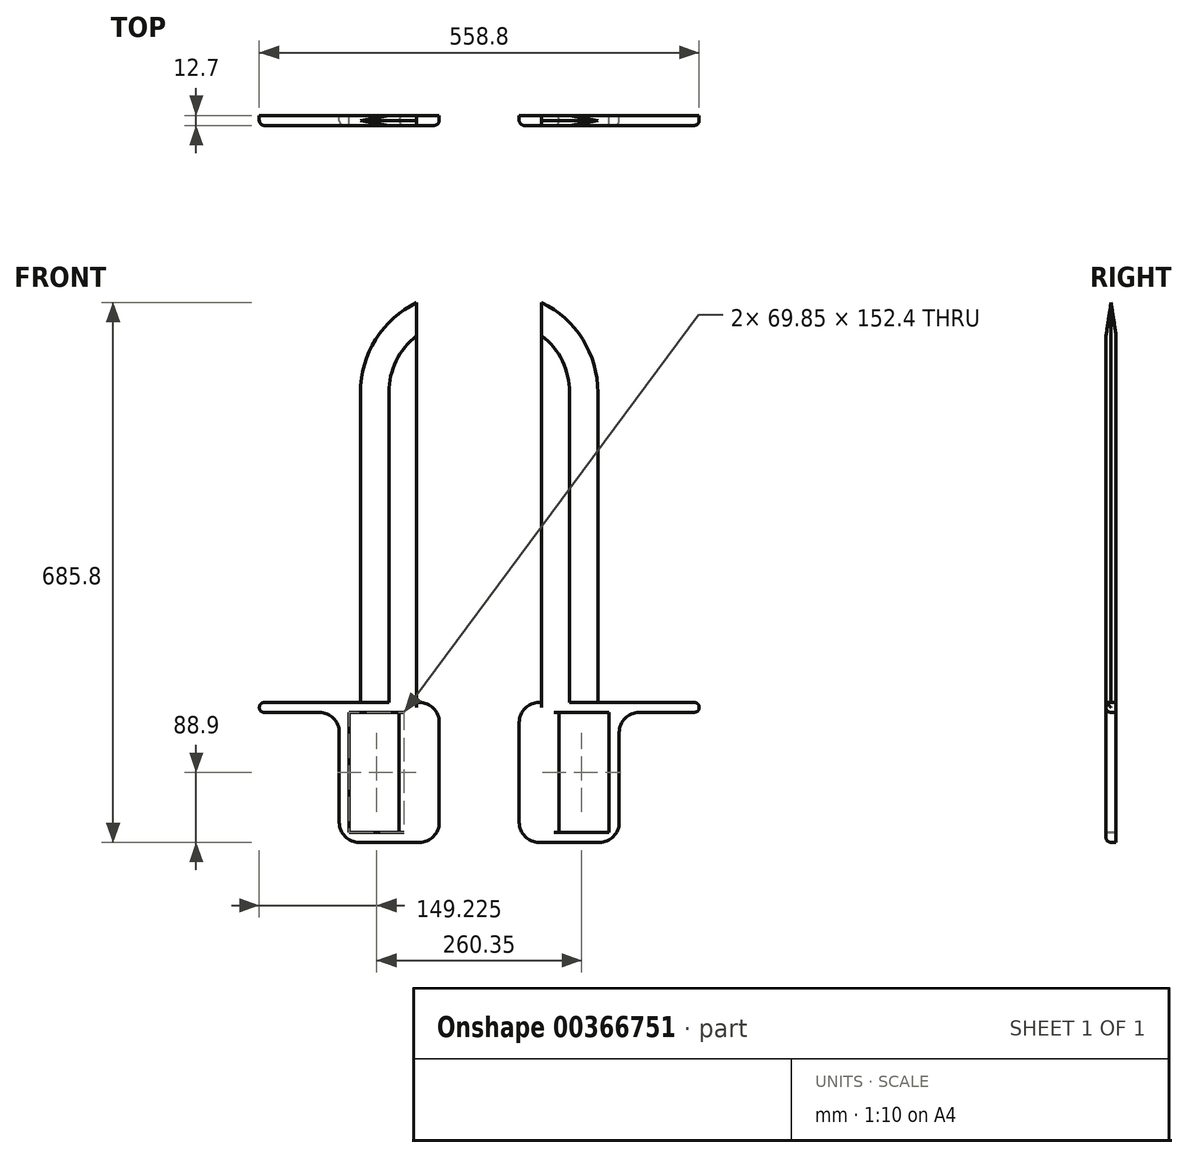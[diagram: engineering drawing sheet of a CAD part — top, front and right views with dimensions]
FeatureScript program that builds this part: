
annotation { "Feature Type Name" : "Feature", "Feature Type Description" : "" }
export const myFeature = defineFeature(function(context is Context, id is Id, definition is map)
    precondition{}
    {
        {
            var Q0;
            Q0=qCreatedBy(makeId("Front.planeOp"),FACE);
            var sketch = newSketch(context, id + "F0", { "sketchPlane" : qUnion([Q0])});
            skLineSegment(sketch, "E0", {"start": v(0, 0) * mm, "end": v(-76.2, 0) * mm});
            skLineSegment(sketch, "E1.bottom", {"start": v(-50.8, -76.2) * mm, "end": v(-101.6, -76.2) * mm});
            skLineSegment(sketch, "E1.top", {"start": v(-50.8, 76.2) * mm, "end": v(-101.6, 76.2) * mm});
            skLineSegment(sketch, "E1.left", {"start": v(-50.8, -76.2) * mm, "end": v(-50.8, 76.2) * mm});
            skLineSegment(sketch, "E1.right", {"start": v(-101.6, -76.2) * mm, "end": v(-101.6, 76.2) * mm});
            skPoint(sketch, "E1.middle", {"position": v(-76.2, 0) * mm});
            skLineSegment(sketch, "E2", {"start": v(-50.8, 76.2) * mm, "end": v(-50.8, 88.9) * mm});
            skLineSegment(sketch, "E3", {"start": v(-50.8, 88.9) * mm, "end": v(-177.8, 88.9) * mm});
            skLineSegment(sketch, "E4", {"start": v(-101.6, 76.2) * mm, "end": v(-165.1, 76.2) * mm});
            skLineSegment(sketch, "E5", {"start": v(-177.8, 88.9) * mm, "end": v(-177.8, -88.9) * mm});
            skLineSegment(sketch, "E6", {"start": v(-165.1, 76.2) * mm, "end": v(-165.1, -76.2) * mm});
            skLineSegment(sketch, "E7", {"start": v(-165.1, -76.2) * mm, "end": v(-101.6, -76.2) * mm});
            skLineSegment(sketch, "E8", {"start": v(-177.8, -88.9) * mm, "end": v(-50.8, -88.9) * mm});
            skLineSegment(sketch, "E9", {"start": v(-50.8, -76.2) * mm, "end": v(-50.8, -88.9) * mm});
            skLineSegment(sketch, "E10", {"start": v(-165.1, 76.2) * mm, "end": v(-279.4, 76.2) * mm});
            skLineSegment(sketch, "E11", {"start": v(-177.8, 88.9) * mm, "end": v(-279.4, 88.9) * mm});
            skLineSegment(sketch, "E12", {"start": v(-279.4, 88.9) * mm, "end": v(-279.4, 76.2) * mm});
            skSolve(sketch);
        }
        {
            var Q0;
            Q0 = qSketchRegion(id + "F0", true);
            extrude(context, id + "F1", {"entities" : qUnion([Q0]), "depth" : 12.7 * mm});
        }
        {
            var Q0;
            Q0=makeQuery(id+"F1.opExtrude","CAP_FACE",FACE,{"disambiguationData":[OSD([sQuery(id+"F0.wireOp",EDGE,"E1.left"),sQuery(id+"F0.wireOp",EDGE,"E1.right"),sQuery(id+"F0.wireOp",EDGE,"E2"),sQuery(id+"F0.wireOp",EDGE,"E3"),sQuery(id+"F0.wireOp",EDGE,"E4"),sQuery(id+"F0.wireOp",EDGE,"E5"),sQuery(id+"F0.wireOp",EDGE,"E6"),sQuery(id+"F0.wireOp",EDGE,"E7"),sQuery(id+"F0.wireOp",EDGE,"E8"),sQuery(id+"F0.wireOp",EDGE,"E9")])],"isStart":false});
            var sketch = newSketch(context, id + "F2", { "sketchPlane" : qUnion([Q0])});
            skLineSegment(sketch, "E13", {"start": v(-50.8, 88.9) * mm, "end": v(-50.8, 88.9) * mm});
            skLineSegment(sketch, "E14", {"start": v(-50.8, 88.9) * mm, "end": v(-165.1, 88.9) * mm});
            skLineSegment(sketch, "E15", {"start": v(-165.1, 88.9) * mm, "end": v(-107.95, 88.9) * mm});
            skLineSegment(sketch, "E16", {"start": v(-50.8, 88.9) * mm, "end": v(-107.95, 88.9) * mm});
            skLineSegment(sketch, "E17", {"start": v(-107.95, 88.9) * mm, "end": v(-50.8, 88.9) * mm});
            skLineSegment(sketch, "E18", {"start": v(-79.37, 88.9) * mm, "end": v(-107.95, 88.9) * mm});
            skLineSegment(sketch, "E19", {"start": v(-50.8, 88.9) * mm, "end": v(-79.37, 88.9) * mm});
            skLineSegment(sketch, "E20", {"start": v(-79.37, 88.9) * mm, "end": v(-79.37, 596.9) * mm});
            skLineSegment(sketch, "E21", {"start": v(-79.37, 596.9) * mm, "end": v(-79.37, 596.9) * mm});
            skLineSegment(sketch, "E22", {"start": v(-107.95, 88.9) * mm, "end": v(-136.52, 88.9) * mm});
            skLineSegment(sketch, "E23", {"start": v(-136.52, 88.9) * mm, "end": v(-165.1, 88.9) * mm});
            skLineSegment(sketch, "E24", {"start": v(-165.1, 88.9) * mm, "end": v(-150.81, 88.9) * mm});
            skLineSegment(sketch, "E25", {"start": v(-150.81, 88.9) * mm, "end": v(-150.81, 596.9) * mm});
            skLineSegment(sketch, "E26", {"start": v(-79.37, 596.9) * mm, "end": v(-150.81, 596.9) * mm});
            skSolve(sketch);
        }
        {
            var Q0;
            Q0 = qSketchRegion(id + "F2", true);
            extrude(context, id + "F3", {"entities" : qUnion([Q0]), "operationType" : NewBodyOperationType.ADD, "depth" : -12.7 * mm});
        }
        {
            var Q0;
            Q0=makeQuery(id+"F3.opExtrude","SWEPT_EDGE",EDGE,{"disambiguationData":[OSD([sQuery(id+"F2.wireOp",EDGE,"E25"),sQuery(id+"F2.wireOp",EDGE,"E26")])]});
            fillet(context, id + "F4", {"entities" : qUnion([Q0]), "radius" : 127 * mm, "tangentPropagation" : true, "allowEdgeOverflow" : false});
        }
        {
            var Q0;
            Q0=makeQuery(id+"F1.opExtrude","CAP_EDGE",EDGE,{"disambiguationData":[OSD([sQuery(id+"F0.wireOp",EDGE,"E1.right")])],"isStart":false});
            var Q1;
            Q1=makeQuery(id+"F1.opExtrude","CAP_EDGE",EDGE,{"disambiguationData":[OSD([sQuery(id+"F0.wireOp",EDGE,"E1.right")])],"isStart":true});
            fillet(context, id + "F5", {"entities" : qUnion([Q0, Q1]), "radius" : 6.35 * mm, "tangentPropagation" : true, "allowEdgeOverflow" : false});
        }
        {
            var Q0;
            Q0=makeQuery(id+"F1.opExtrude","SWEPT_EDGE",EDGE,{"disambiguationData":[OSD([sQuery(id+"F0.wireOp",EDGE,"E3"),sQuery(id+"F0.wireOp",EDGE,"E5")])]});
            var Q1;
            Q1=makeQuery(id+"F1.opExtrude","SWEPT_EDGE",EDGE,{"disambiguationData":[OSD([sQuery(id+"F0.wireOp",EDGE,"E2"),sQuery(id+"F0.wireOp",EDGE,"E3")])]});
            var Q2;
            Q2=makeQuery(id+"F1.opExtrude","SWEPT_EDGE",EDGE,{"disambiguationData":[OSD([sQuery(id+"F0.wireOp",EDGE,"E8"),sQuery(id+"F0.wireOp",EDGE,"E9")])]});
            var Q3;
            Q3=makeQuery(id+"F1.opExtrude","SWEPT_EDGE",EDGE,{"disambiguationData":[OSD([sQuery(id+"F0.wireOp",EDGE,"E5"),sQuery(id+"F0.wireOp",EDGE,"E8")])]});
            fillet(context, id + "F6", {"entities" : qUnion([Q0, Q1, Q2, Q3]), "radius" : 25.4 * mm, "tangentPropagation" : true, "allowEdgeOverflow" : false});
        }
        {
            var Q0;
            Q0=makeQuery(id+"F1.opExtrude","CAP_EDGE",EDGE,{"disambiguationData":[OSD([sQuery(id+"F0.wireOp",EDGE,"E1.left"),sQuery(id+"F0.wireOp",EDGE,"E2"),sQuery(id+"F0.wireOp",EDGE,"E9")])],"isStart":false});
            fillet(context, id + "F7", {"entities" : qUnion([Q0]), "radius" : 6.35 * mm, "tangentPropagation" : true, "allowEdgeOverflow" : false});
        }
        {
            var Q0;
            Q0=makeQuery(id+"F1.opExtrude","CAP_EDGE",EDGE,{"disambiguationData":[OSD([sQuery(id+"F0.wireOp",EDGE,"E12")])],"isStart":false});
            var Q1;
            Q1=makeQuery(id+"F1.opExtrude","SWEPT_EDGE",EDGE,{"disambiguationData":[OSD([sQuery(id+"F0.wireOp",EDGE,"E11"),sQuery(id+"F0.wireOp",EDGE,"E12")])]});
            fillet(context, id + "F8", {"entities" : qUnion([Q0, Q1]), "radius" : 6.35 * mm, "tangentPropagation" : true, "allowEdgeOverflow" : false});
        }
        {
            var Q0;
            Q0=makeQuery(id+"F3.opExtrude","CAP_EDGE",EDGE,{"disambiguationData":[OSD([sQuery(id+"F2.wireOp",EDGE,"E25")])],"isStart":true});
            var Q1;
            Q1=makeQuery(id+"F3.opExtrude","CAP_EDGE",EDGE,{"disambiguationData":[OSD([sQuery(id+"F2.wireOp",EDGE,"E25")])],"isStart":false});
            chamfer(context, id + "F9", {"entities" : qUnion([Q0, Q1]), "chamferType" : ChamferType.OFFSET_ANGLE, "width" : 6.35 * mm, "oppositeDirection" : false, "angle" : 80 * degree, "tangentPropagation" : true});
        }
        {
            var Q0;
            Q0=makeQuery(id+"F1.opExtrude","SWEPT_BODY",BODY,{"disambiguationData":[OSD([sQuery(id+"F0.wireOp",EDGE,"E1.left"),sQuery(id+"F0.wireOp",EDGE,"E1.right"),sQuery(id+"F0.wireOp",EDGE,"E2"),sQuery(id+"F0.wireOp",EDGE,"E3"),sQuery(id+"F0.wireOp",EDGE,"E4"),sQuery(id+"F0.wireOp",EDGE,"E5"),sQuery(id+"F0.wireOp",EDGE,"E6"),sQuery(id+"F0.wireOp",EDGE,"E7"),sQuery(id+"F0.wireOp",EDGE,"E8"),sQuery(id+"F0.wireOp",EDGE,"E9"),sQuery(id+"F0.wireOp",EDGE,"E10"),sQuery(id+"F0.wireOp",EDGE,"E11"),sQuery(id+"F0.wireOp",EDGE,"E12")])]});
            var Q1;
            Q1=qCreatedBy(makeId("Right.planeOp"),FACE);
            mirror(context, id + "F10", {"entities" : qUnion([Q0]), "mirrorPlane" : qUnion([Q1])});
        }
    });
